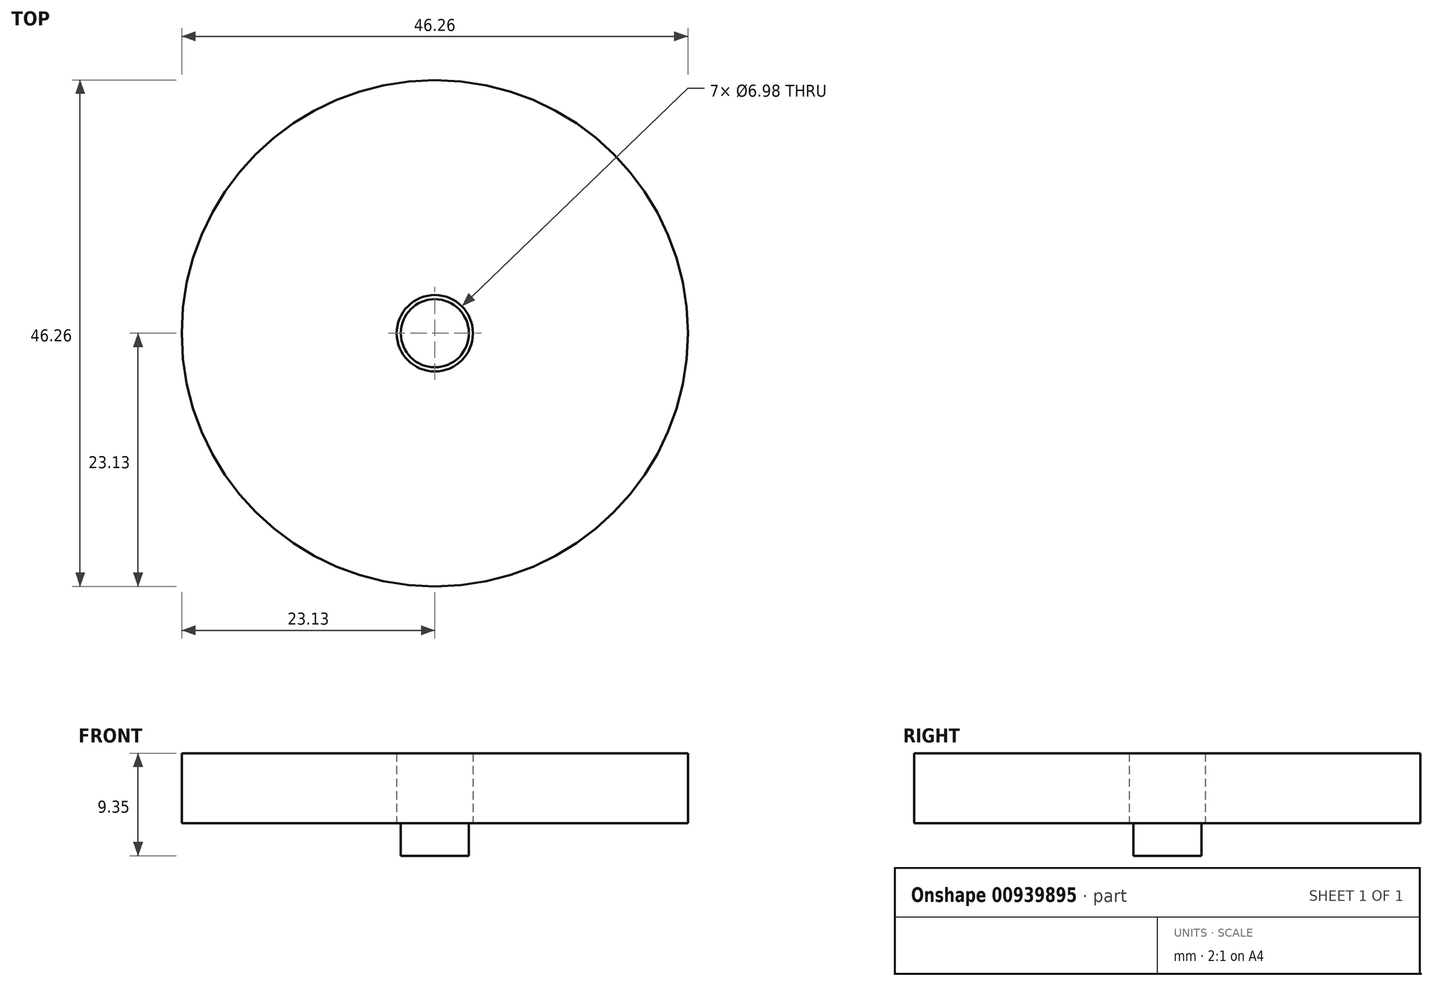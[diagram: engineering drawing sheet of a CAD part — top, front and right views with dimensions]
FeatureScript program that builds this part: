
annotation { "Feature Type Name" : "Feature", "Feature Type Description" : "" }
export const myFeature = defineFeature(function(context is Context, id is Id, definition is map)
    precondition{}
    {
        {
            var Q0;
            Q0=qCreatedBy(makeId("Top.planeOp"),FACE);
            var sketch = newSketch(context, id + "F0", { "sketchPlane" : qUnion([Q0])});
            skCircle(sketch, "E0", {"center": v(0, 0) * mm, "radius": 23.13 * mm});
            skCircle(sketch, "E1", {"center": v(0, 0) * mm, "radius": 3.49 * mm});
            skCircle(sketch, "E2", {"center": v(0, 0) * mm, "radius": 3.11 * mm});
            skPoint(sketch, "E3.orphan", {"position": v(-22.99, -22.99) * mm});
            skPoint(sketch, "E4.end.orphan", {"position": v(0, -32.51) * mm});
            skSolve(sketch);
        }
        {
            var Q0;
            {var subQ0=sQuery(id+"F0.wireOp",EDGE,"624a3082-f0bd-489e-bac8-f56769b1647d.1.7.0");Q0=makeQuery(id+"F0.imprint","IMPRINT",FACE,{"disambiguationData":[TD([[makeQuery(id+"F0.imprint","IMPRINT",EDGE,{"derivedFrom":subQ0}),-1.0]])]});}
            var Q1;
            {var subQ0=sQuery(id+"F0.wireOp",EDGE,"624a3082-f0bd-489e-bac8-f56769b1647d.1.6.0");Q1=makeQuery(id+"F0.imprint","IMPRINT",FACE,{"disambiguationData":[TD([[makeQuery(id+"F0.imprint","IMPRINT",EDGE,{"derivedFrom":subQ0}),-1.0]])]});}
            var Q2;
            {var subQ0=sQuery(id+"F0.wireOp",EDGE,"7d7c321b-5e5e-4767-a6c6-7154afb0b3740.MirrorCS");Q2=makeQuery(id+"F0.imprint","IMPRINT",FACE,{"disambiguationData":[TD([[makeQuery(id+"F0.imprint","IMPRINT",EDGE,{"derivedFrom":subQ0}),1.0]])]});}
            var Q3;
            {var subQ0=sQuery(id+"F0.wireOp",EDGE,"6a3865bb-d3f2-4b20-aa9e-75a6c40126ac.3.0");Q3=makeQuery(id+"F0.imprint","IMPRINT",FACE,{"disambiguationData":[TD([[makeQuery(id+"F0.imprint","IMPRINT",EDGE,{"derivedFrom":subQ0}),-1.0]])]});}
            var Q4;
            {var subQ0=sQuery(id+"F0.wireOp",EDGE,"E0");var subQ8=makeQuery(id+"F0.imprint","INTERSECT",VERTEX,{"derivedFrom":[subQ0,sQuery(id+"F0.wireOp",EDGE,"624a3082-f0bd-489e-bac8-f56769b1647d.1.6.0")]});Q4=makeQuery(id+"F0.imprint","IMPRINT",FACE,{"disambiguationData":[TD([[makeQuery(id+"F0.imprint","IMPRINT",EDGE,{"disambiguationData":[TD([[subQ8,-1.0]])],"derivedFrom":subQ0}),1.0]])]});}
            var Q5;
            {var subQ0=sQuery(id+"F0.wireOp",EDGE,"601a7b0d-6f46-43de-a6f4-66336205a0b90.MirrorCS");Q5=makeQuery(id+"F0.imprint","IMPRINT",FACE,{"disambiguationData":[TD([[makeQuery(id+"F0.imprint","IMPRINT",EDGE,{"derivedFrom":subQ0}),1.0]])]});}
            var Q6;
            {var subQ0=sQuery(id+"F0.wireOp",EDGE,"6a3865bb-d3f2-4b20-aa9e-75a6c40126ac.1.0");Q6=makeQuery(id+"F0.imprint","IMPRINT",FACE,{"disambiguationData":[TD([[makeQuery(id+"F0.imprint","IMPRINT",EDGE,{"derivedFrom":subQ0}),-1.0]])]});}
            var Q7;
            {var subQ0=sQuery(id+"F0.wireOp",EDGE,"659b57cc-cec8-43e7-9b27-b471c0e5487a0.MirrorCS");Q7=makeQuery(id+"F0.imprint","IMPRINT",FACE,{"disambiguationData":[TD([[makeQuery(id+"F0.imprint","IMPRINT",EDGE,{"derivedFrom":subQ0}),-1.0]])]});}
            var Q8;
            {var subQ0=sQuery(id+"F0.wireOp",EDGE,"93301f7c-61fb-474a-a0c9-4264b807d700.1.5.0");Q8=makeQuery(id+"F0.imprint","IMPRINT",FACE,{"disambiguationData":[TD([[makeQuery(id+"F0.imprint","IMPRINT",EDGE,{"derivedFrom":subQ0}),-1.0]])]});}
            extrude(context, id + "F1", {"entities" : qUnion([Q0, Q1, Q2, Q3, Q4, Q5, Q6, Q7, Q8]), "depth" : 6.38 * mm, "offsetDistance" : 25.4 * mm});
        }
        {
            var Q0;
            Q0=makeQuery(id+"F0.imprint","IMPRINT",FACE,{"disambiguationData":[TD([[makeQuery(id+"F0.imprint","IMPRINT",EDGE,{"derivedFrom":sQuery(id+"F0.wireOp",EDGE,"E2")}),1.0]])]});
            extrude(context, id + "F2", {"entities" : qUnion([Q0]), "oppositeDirection" : true, "depth" : 2.97 * mm, "offsetDistance" : 25.4 * mm});
        }
    });
